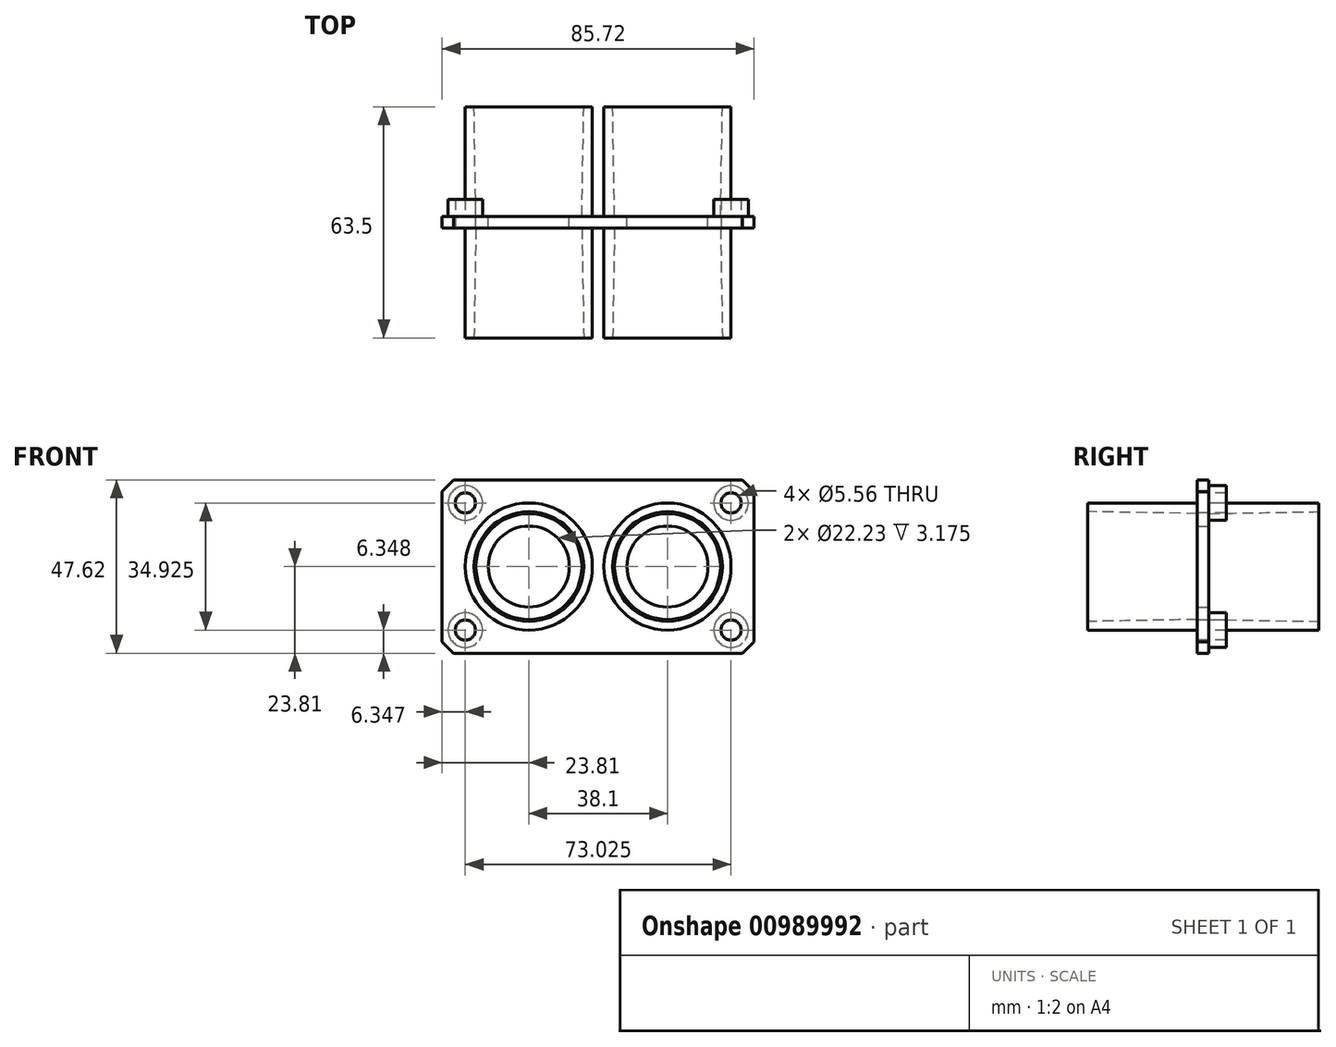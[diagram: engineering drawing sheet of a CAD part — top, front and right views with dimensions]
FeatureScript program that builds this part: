
annotation { "Feature Type Name" : "Feature", "Feature Type Description" : "" }
export const myFeature = defineFeature(function(context is Context, id is Id, definition is map)
    precondition{}
    {
        {
            var Q0;
            Q0=qCreatedBy(makeId("Front.planeOp"),FACE);
            var sketch = newSketch(context, id + "F0", { "sketchPlane" : qUnion([Q0])});
            skLineSegment(sketch, "E0.bottom", {"start": v(-42.86, 23.81) * mm, "end": v(42.86, 23.81) * mm});
            skLineSegment(sketch, "E0.top", {"start": v(-42.86, -23.81) * mm, "end": v(42.86, -23.81) * mm});
            skLineSegment(sketch, "E0.left", {"start": v(-42.86, 23.81) * mm, "end": v(-42.86, -23.81) * mm});
            skLineSegment(sketch, "E0.right", {"start": v(42.86, 23.81) * mm, "end": v(42.86, -23.81) * mm});
            skPoint(sketch, "E0.middle", {"position": v(0, 0) * mm});
            skLineSegment(sketch, "E1", {"start": v(-19.05, 0) * mm, "end": v(19.05, 0) * mm});
            skCircle(sketch, "E2", {"center": v(19.05, 0) * mm, "radius": 17.46 * mm});
            skCircle(sketch, "E3", {"center": v(-19.05, 0) * mm, "radius": 17.46 * mm});
            skCircle(sketch, "E4", {"center": v(-19.05, 0) * mm, "radius": 23.81 * mm, "construction": true});
            skLineSegment(sketch, "E5.0", {"start": v(-36.51, 17.46) * mm, "end": v(36.51, 17.46) * mm});
            skLineSegment(sketch, "E5.1", {"start": v(-36.51, 17.46) * mm, "end": v(-36.51, -17.46) * mm});
            skLineSegment(sketch, "E5.2", {"start": v(-36.51, -17.46) * mm, "end": v(36.51, -17.46) * mm});
            skLineSegment(sketch, "E5.3", {"start": v(36.51, 17.46) * mm, "end": v(36.51, -17.46) * mm});
            skCircle(sketch, "E6", {"center": v(-36.51, 17.46) * mm, "radius": 6.35 * mm, "construction": true});
            skCircle(sketch, "E7", {"center": v(-36.51, 17.46) * mm, "radius": 2.25 * mm});
            skCircle(sketch, "E8", {"center": v(-36.51, 17.46) * mm, "radius": 3.97 * mm});
            skLineSegment(sketch, "E9", {"start": v(-39.69, 23.81) * mm, "end": v(-42.86, 20.64) * mm});
            skCircle(sketch, "E10", {"center": v(-19.05, 0) * mm, "radius": 15.08 * mm});
            skCircle(sketch, "E11", {"center": v(19.05, 0) * mm, "radius": 15.08 * mm});
            skCircle(sketch, "E12", {"center": v(-19.05, 0) * mm, "radius": 11.11 * mm});
            skCircle(sketch, "E13", {"center": v(19.05, 0) * mm, "radius": 11.11 * mm});
            skCircle(sketch, "E14", {"center": v(19.05, 0) * mm, "radius": 23.81 * mm});
            skCircle(sketch, "E15", {"center": v(-36.51, -17.46) * mm, "radius": 2.25 * mm});
            skCircle(sketch, "E16", {"center": v(36.51, 17.46) * mm, "radius": 2.25 * mm});
            skCircle(sketch, "E17", {"center": v(36.51, -17.46) * mm, "radius": 2.25 * mm});
            skCircle(sketch, "E18", {"center": v(-36.51, 17.46) * mm, "radius": 4.76 * mm});
            skCircle(sketch, "E19", {"center": v(-36.51, -17.46) * mm, "radius": 4.76 * mm});
            skCircle(sketch, "E20", {"center": v(36.51, 17.46) * mm, "radius": 4.76 * mm});
            skCircle(sketch, "E21", {"center": v(36.51, -17.46) * mm, "radius": 4.76 * mm});
            skCircle(sketch, "E22", {"center": v(-36.51, 17.46) * mm, "radius": 2.78 * mm, "construction": true});
            skCircle(sketch, "E23", {"center": v(-36.51, -17.46) * mm, "radius": 2.78 * mm, "construction": true});
            skCircle(sketch, "E24", {"center": v(36.51, 17.46) * mm, "radius": 2.78 * mm, "construction": true});
            skCircle(sketch, "E25", {"center": v(36.51, -17.46) * mm, "radius": 2.78 * mm, "construction": true});
            skSolve(sketch);
        }
        {
            var Q0;
            Q0=qCreatedBy(makeId("Right.planeOp"),FACE);
            var Q1;
            Q1=sQuery(id+"F0.wireOp",VERTEX,"E1.start");
            cPlane(context, id + "F1", {"entities" : qUnion([Q0, Q1]), "cplaneType" : CPlaneType.PLANE_POINT, "offset" : 25.4 * mm, "width" : 152.4 * mm, "height" : 152.4 * mm});
        }
        {
            var Q0;
            Q0=qCreatedBy(makeId("Right.planeOp"),FACE);
            var Q1;
            Q1=sQuery(id+"F0.wireOp",VERTEX,"E1.end");
            cPlane(context, id + "F2", {"entities" : qUnion([Q0, Q1]), "cplaneType" : CPlaneType.PLANE_POINT, "offset" : 25.4 * mm, "width" : 152.4 * mm, "height" : 152.4 * mm});
        }
        {
            var Q0;
            Q0=qCreatedBy(id+"F1.planeOp",FACE);
            var sketch = newSketch(context, id + "F3", { "sketchPlane" : qUnion([Q0])});
            skLineSegment(sketch, "E26", {"start": v(-30.16, 0) * mm, "end": v(12.8, 0) * mm, "construction": true});
            skLineSegment(sketch, "E27", {"start": v(-30.16, 17.46) * mm, "end": v(-30.16, -17.46) * mm});
            skLineSegment(sketch, "E28", {"start": v(-30.16, 15.08) * mm, "end": v(-30.16, -15.08) * mm});
            skLineSegment(sketch, "E29", {"start": v(-30.16, 15.08) * mm, "end": v(0, 14.55) * mm});
            skLineSegment(sketch, "E30", {"start": v(0, 14.55) * mm, "end": v(0, -14.55) * mm});
            skLineSegment(sketch, "E31", {"start": v(0, -14.55) * mm, "end": v(-30.16, -15.08) * mm});
            skLineSegment(sketch, "E32", {"start": v(-30.16, 17.46) * mm, "end": v(0, 17.46) * mm});
            skLineSegment(sketch, "E33", {"start": v(0, 17.46) * mm, "end": v(0, 23.81) * mm});
            skLineSegment(sketch, "E34", {"start": v(0, 23.81) * mm, "end": v(3.17, 23.81) * mm});
            skLineSegment(sketch, "E35", {"start": v(3.17, 23.81) * mm, "end": v(3.18, -23.81) * mm});
            skLineSegment(sketch, "E36", {"start": v(-30.16, -17.46) * mm, "end": v(0, -17.46) * mm});
            skLineSegment(sketch, "E37", {"start": v(0, -17.46) * mm, "end": v(0, -23.81) * mm});
            skLineSegment(sketch, "E38", {"start": v(0, -23.81) * mm, "end": v(3.18, -23.81) * mm});
            skLineSegment(sketch, "E39", {"start": v(3.17, 17.46) * mm, "end": v(33.34, 17.46) * mm});
            skLineSegment(sketch, "E40", {"start": v(33.34, 17.46) * mm, "end": v(33.34, 15.08) * mm});
            skLineSegment(sketch, "E41", {"start": v(33.34, 15.08) * mm, "end": v(3.17, 14.55) * mm});
            skSolve(sketch);
        }
        {
            var Q0;
            Q0=qCreatedBy(makeId("Front.planeOp"),FACE);
            var sketch = newSketch(context, id + "F4", { "sketchPlane" : qUnion([Q0])});
            skLineSegment(sketch, "E42.0", {"start": v(-42.86, 23.81) * mm, "end": v(42.86, 23.81) * mm});
            skLineSegment(sketch, "E42.1", {"start": v(42.86, 23.81) * mm, "end": v(42.86, -23.81) * mm});
            skLineSegment(sketch, "E42.2", {"start": v(-42.86, -23.81) * mm, "end": v(42.86, -23.81) * mm});
            skLineSegment(sketch, "E42.3", {"start": v(-42.86, 23.81) * mm, "end": v(-42.86, -23.81) * mm});
            skSolve(sketch);
        }
        {
            var Q0;
            Q0=qSketchRegion(id+"F4",true);
            var Q1;
            Q1=sQuery(id+"F3.wireOp",VERTEX,"E34.end");
            extrude(context, id + "F5", {"entities" : qUnion([Q0]), "endBound" : BoundingType.UP_TO_VERTEX, "oppositeDirection" : true, "depth" : 25.4 * mm, "endBoundEntityVertex" : qUnion([Q1]), "offsetDistance" : 25.4 * mm});
        }
        {
            var Q0;
            Q0=qCreatedBy(makeId("Front.planeOp"),FACE);
            var sketch = newSketch(context, id + "F6", { "sketchPlane" : qUnion([Q0])});
            skCircle(sketch, "E43.0", {"center": v(19.05, 0) * mm, "radius": 17.46 * mm});
            skCircle(sketch, "E43.1", {"center": v(-19.05, 0) * mm, "radius": 17.46 * mm});
            skSolve(sketch);
        }
        {
            var Q0;
            Q0=qSketchRegion(id+"F6",true);
            var Q1;
            Q1=sQuery(id+"F3.wireOp",VERTEX,"E27.start");
            extrude(context, id + "F7", {"entities" : qUnion([Q0]), "operationType" : NewBodyOperationType.ADD, "endBound" : BoundingType.UP_TO_VERTEX, "depth" : 25.4 * mm, "endBoundEntityVertex" : qUnion([Q1]), "offsetDistance" : 25.4 * mm});
        }
        {
            var Q0;
            Q0=qCreatedBy(makeId("Front.planeOp"),FACE);
            var sketch = newSketch(context, id + "F8", { "sketchPlane" : qUnion([Q0])});
            skCircle(sketch, "E44.0", {"center": v(19.05, 0) * mm, "radius": 17.46 * mm});
            skCircle(sketch, "E44.1", {"center": v(-19.05, 0) * mm, "radius": 17.46 * mm});
            skSolve(sketch);
        }
        {
            var Q0;
            Q0=qSketchRegion(id+"F8",true);
            var Q1;
            Q1=sQuery(id+"F3.wireOp",VERTEX,"E39.end");
            extrude(context, id + "F9", {"entities" : qUnion([Q0]), "operationType" : NewBodyOperationType.ADD, "endBound" : BoundingType.UP_TO_VERTEX, "oppositeDirection" : true, "depth" : 25.4 * mm, "endBoundEntityVertex" : qUnion([Q1]), "offsetDistance" : 25.4 * mm});
        }
        {
            var Q0;
            Q0=qCreatedBy(id+"F1.planeOp",FACE);
            var sketch = newSketch(context, id + "F10", { "sketchPlane" : qUnion([Q0])});
            skLineSegment(sketch, "E45.0", {"start": v(-37.2, 15.2) * mm, "end": v(0, 14.55) * mm});
            skLineSegment(sketch, "E45.1", {"start": v(0, 14.55) * mm, "end": v(0, 11.11) * mm});
            skLineSegment(sketch, "E45.2", {"start": v(-37.2, 0) * mm, "end": v(35.4, 0) * mm});
            skLineSegment(sketch, "E46", {"start": v(0, 11.11) * mm, "end": v(3.17, 11.11) * mm});
            skLineSegment(sketch, "E47", {"start": v(3.17, 11.11) * mm, "end": v(3.17, 14.55) * mm});
            skLineSegment(sketch, "E48.0", {"start": v(35.4, 15.12) * mm, "end": v(3.17, 14.55) * mm});
            skPoint(sketch, "E49.orphan", {"position": v(12.8, 0) * mm});
            skPoint(sketch, "E50.orphan", {"position": v(33.34, 15.08) * mm});
            skPoint(sketch, "E51.orphan", {"position": v(-30.16, 15.08) * mm});
            skPoint(sketch, "E52.orphan", {"position": v(-30.16, 0) * mm});
            skLineSegment(sketch, "E53", {"start": v(35.4, 15.12) * mm, "end": v(35.4, 0) * mm});
            skLineSegment(sketch, "E54", {"start": v(-37.2, 15.2) * mm, "end": v(-37.2, 0) * mm});
            skPoint(sketch, "E55.orphan", {"position": v(0, -14.55) * mm});
            skSolve(sketch);
        }
        {
            var Q0;
            Q0=qCreatedBy(id+"F2.planeOp",FACE);
            var sketch = newSketch(context, id + "F11", { "sketchPlane" : qUnion([Q0])});
            skLineSegment(sketch, "E56.0", {"start": v(-37.2, 15.2) * mm, "end": v(0, 14.55) * mm});
            skLineSegment(sketch, "E56.1", {"start": v(0, 14.55) * mm, "end": v(0, 11.11) * mm});
            skLineSegment(sketch, "E56.2", {"start": v(0, 11.11) * mm, "end": v(3.17, 11.11) * mm});
            skLineSegment(sketch, "E56.3", {"start": v(3.17, 11.11) * mm, "end": v(3.17, 14.55) * mm});
            skLineSegment(sketch, "E56.4", {"start": v(35.4, 15.12) * mm, "end": v(3.17, 14.55) * mm});
            skLineSegment(sketch, "E56.5", {"start": v(-37.2, 0) * mm, "end": v(35.4, 0) * mm});
            skLineSegment(sketch, "E56.6", {"start": v(35.4, 15.12) * mm, "end": v(35.4, 0) * mm});
            skLineSegment(sketch, "E56.7", {"start": v(-37.2, 15.2) * mm, "end": v(-37.2, 0) * mm});
            skSolve(sketch);
        }
        {
            var Q0;
            Q0=qSketchRegion(id+"F10",true);
            var Q1;
            Q1=sQuery(id+"F10.wireOp",EDGE,"E45.2");
            revolve(context, id + "F12", {"operationType" : NewBodyOperationType.REMOVE, "surfaceOperationType" : NewSurfaceOperationType.NEW, "entities" : qUnion([Q0]), "axis" : qUnion([Q1]), "revolveType" : RevolveType.FULL, "oppositeDirection" : true});
        }
        {
            var Q0;
            Q0=qSketchRegion(id+"F11",true);
            var Q1;
            Q1=sQuery(id+"F11.wireOp",EDGE,"E56.5");
            revolve(context, id + "F13", {"operationType" : NewBodyOperationType.REMOVE, "surfaceOperationType" : NewSurfaceOperationType.NEW, "entities" : qUnion([Q0]), "axis" : qUnion([Q1]), "revolveType" : RevolveType.FULL, "oppositeDirection" : true});
        }
        {
            var Q0;
            Q0=makeQuery(id+"F5.opExtrude","SWEPT_EDGE",EDGE,{"disambiguationData":[OSD([sQuery(id+"F4.wireOp",EDGE,"E42.0"),sQuery(id+"F4.wireOp",EDGE,"E42.3")])]});
            var Q1;
            Q1=makeQuery(id+"F5.opExtrude","SWEPT_EDGE",EDGE,{"disambiguationData":[OSD([sQuery(id+"F4.wireOp",EDGE,"E42.0"),sQuery(id+"F4.wireOp",EDGE,"E42.1")])]});
            var Q2;
            Q2=makeQuery(id+"F5.opExtrude","SWEPT_EDGE",EDGE,{"disambiguationData":[OSD([sQuery(id+"F4.wireOp",EDGE,"E42.1"),sQuery(id+"F4.wireOp",EDGE,"E42.2")])]});
            var Q3;
            Q3=makeQuery(id+"F5.opExtrude","SWEPT_EDGE",EDGE,{"disambiguationData":[OSD([sQuery(id+"F4.wireOp",EDGE,"E42.2"),sQuery(id+"F4.wireOp",EDGE,"E42.3")])]});
            chamfer(context, id + "F14", {"entities" : qUnion([Q0, Q1, Q2, Q3]), "width" : 3.17 * mm, "tangentPropagation" : true});
        }
        {
            var Q0;
            Q0=qCreatedBy(makeId("Front.planeOp"),FACE);
            var sketch = newSketch(context, id + "F15", { "sketchPlane" : qUnion([Q0])});
            skCircle(sketch, "E57.0", {"center": v(36.51, 17.46) * mm, "radius": 4.76 * mm});
            skCircle(sketch, "E57.1", {"center": v(-36.51, 17.46) * mm, "radius": 4.76 * mm});
            skCircle(sketch, "E57.2", {"center": v(-36.51, -17.46) * mm, "radius": 4.76 * mm});
            skCircle(sketch, "E57.3", {"center": v(36.51, -17.46) * mm, "radius": 4.76 * mm});
            skSolve(sketch);
        }
        {
            var Q0;
            Q0=qSketchRegion(id+"F15",true);
            extrude(context, id + "F16", {"entities" : qUnion([Q0]), "operationType" : NewBodyOperationType.ADD, "oppositeDirection" : true, "depth" : 7.94 * mm, "offsetDistance" : 25.4 * mm});
        }
        {
            var Q0;
            Q0=qCreatedBy(makeId("Front.planeOp"),FACE);
            var sketch = newSketch(context, id + "F17", { "sketchPlane" : qUnion([Q0])});
            skCircle(sketch, "E58.0", {"center": v(-36.51, 17.46) * mm, "radius": 2.78 * mm});
            skCircle(sketch, "E58.1", {"center": v(36.51, 17.46) * mm, "radius": 2.78 * mm});
            skCircle(sketch, "E58.2", {"center": v(-36.51, -17.46) * mm, "radius": 2.78 * mm});
            skCircle(sketch, "E58.3", {"center": v(36.51, -17.46) * mm, "radius": 2.78 * mm});
            skSolve(sketch);
        }
        {
            var Q0;
            Q0=qSketchRegion(id+"F17",true);
            extrude(context, id + "F18", {"entities" : qUnion([Q0]), "operationType" : NewBodyOperationType.REMOVE, "oppositeDirection" : true, "depth" : 25.4 * mm, "offsetDistance" : 25.4 * mm});
        }
    });
